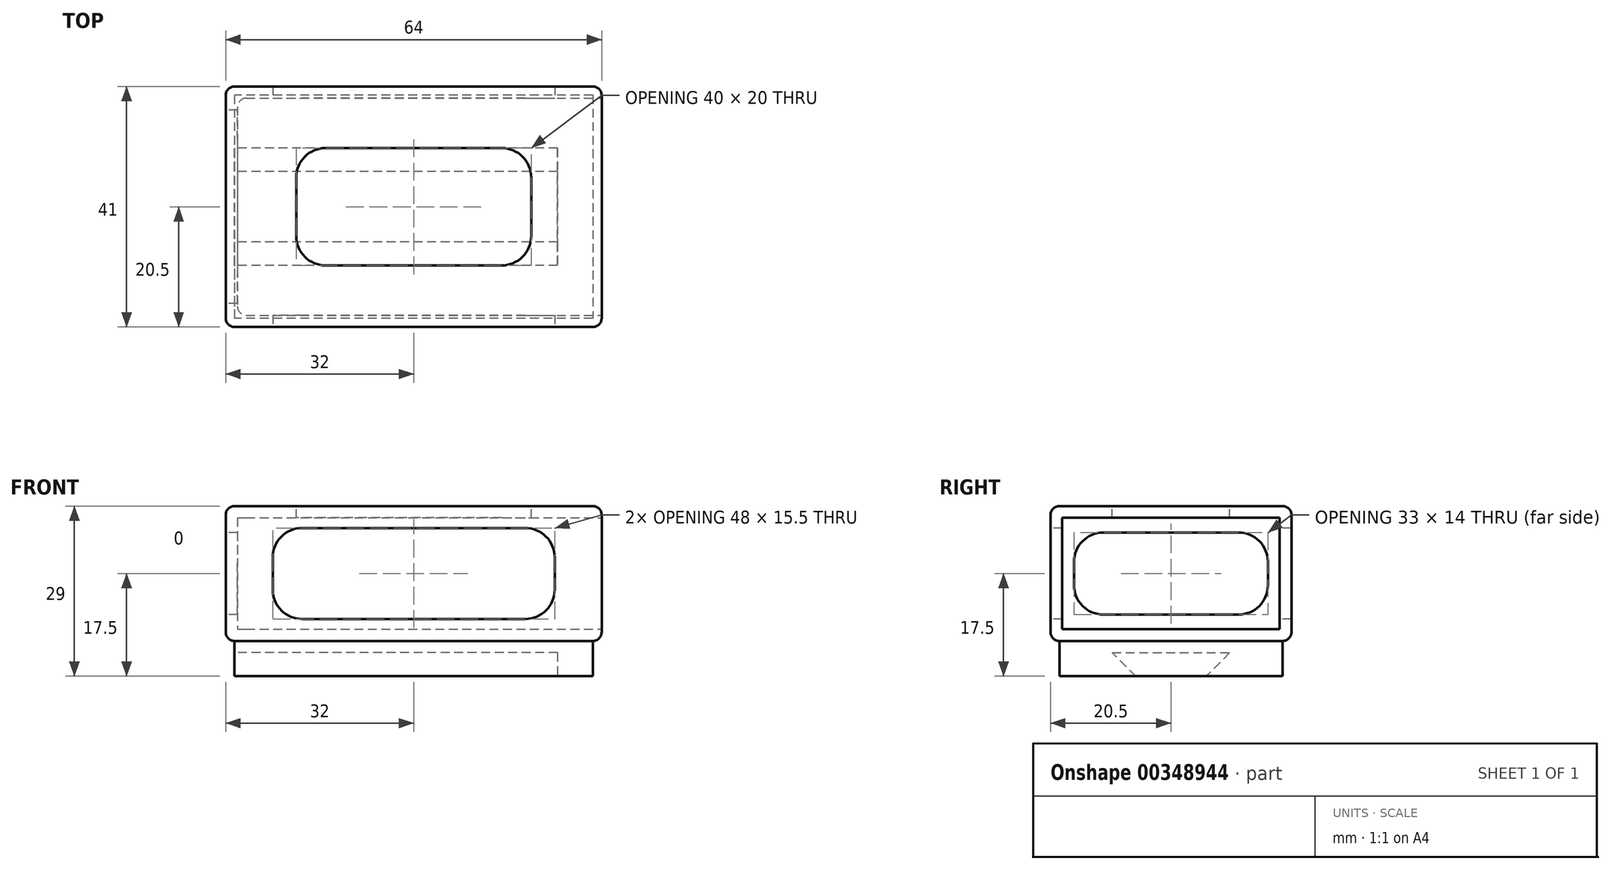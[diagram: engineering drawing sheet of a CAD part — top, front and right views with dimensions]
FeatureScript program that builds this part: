
annotation { "Feature Type Name" : "Feature", "Feature Type Description" : "" }
export const myFeature = defineFeature(function(context is Context, id is Id, definition is map)
    precondition{}
    {
        {
            var Q0;
            Q0=qCreatedBy(makeId("Top.planeOp"),FACE);
            var sketch = newSketch(context, id + "F0", { "sketchPlane" : qUnion([Q0])});
            skLineSegment(sketch, "E0.bottom", {"start": v(32, 20.5) * mm, "end": v(-32, 20.5) * mm});
            skLineSegment(sketch, "E0.top", {"start": v(32, -20.5) * mm, "end": v(-32, -20.5) * mm});
            skLineSegment(sketch, "E0.left", {"start": v(32, 20.5) * mm, "end": v(32, -20.5) * mm});
            skLineSegment(sketch, "E0.right", {"start": v(-32, 20.5) * mm, "end": v(-32, -20.5) * mm});
            skPoint(sketch, "E0.middle", {"position": v(0, 0) * mm});
            skSolve(sketch);
        }
        {
            var Q0;
            Q0=makeQuery(id+"F0.imprint","IMPRINT",FACE,{"disambiguationData":[TD([[makeQuery(id+"F0.imprint","IMPRINT",EDGE,{"derivedFrom":sQuery(id+"F0.wireOp",EDGE,"E0.bottom")}),1.0]])]});
            extrude(context, id + "F1", {"entities" : qUnion([Q0]), "depth" : 11.5 * mm});
        }
        {
            var Q0;
            Q0=makeQuery(id+"F1.opExtrude","CAP_EDGE",EDGE,{"disambiguationData":[OSD([sQuery(id+"F0.wireOp",EDGE,"E0.right")])],"isStart":false});
            var Q1;
            Q1=makeQuery(id+"F1.opExtrude","CAP_EDGE",EDGE,{"disambiguationData":[OSD([sQuery(id+"F0.wireOp",EDGE,"E0.top")])],"isStart":false});
            var Q2;
            Q2=makeQuery(id+"F1.opExtrude","CAP_EDGE",EDGE,{"disambiguationData":[OSD([sQuery(id+"F0.wireOp",EDGE,"E0.left")])],"isStart":false});
            var Q3;
            Q3=makeQuery(id+"F1.opExtrude","CAP_EDGE",EDGE,{"disambiguationData":[OSD([sQuery(id+"F0.wireOp",EDGE,"E0.bottom")])],"isStart":false});
            var Q4;
            Q4=makeQuery(id+"F1.opExtrude","SWEPT_EDGE",EDGE,{"disambiguationData":[OSD([sQuery(id+"F0.wireOp",EDGE,"E0.top"),sQuery(id+"F0.wireOp",EDGE,"E0.left")])]});
            var Q5;
            Q5=makeQuery(id+"F1.opExtrude","SWEPT_EDGE",EDGE,{"disambiguationData":[OSD([sQuery(id+"F0.wireOp",EDGE,"E0.bottom"),sQuery(id+"F0.wireOp",EDGE,"E0.left")])]});
            var Q6;
            Q6=makeQuery(id+"F1.opExtrude","SWEPT_EDGE",EDGE,{"disambiguationData":[OSD([sQuery(id+"F0.wireOp",EDGE,"E0.top"),sQuery(id+"F0.wireOp",EDGE,"E0.right")])]});
            var Q7;
            Q7=makeQuery(id+"F1.opExtrude","SWEPT_EDGE",EDGE,{"disambiguationData":[OSD([sQuery(id+"F0.wireOp",EDGE,"E0.bottom"),sQuery(id+"F0.wireOp",EDGE,"E0.right")])]});
            fillet(context, id + "F2", {"entities" : qUnion([Q0, Q1, Q2, Q3, Q4, Q5, Q6, Q7]), "radius" : 1.5 * mm, "tangentPropagation" : true, "allowEdgeOverflow" : false});
        }
        {
            var Q0;
            Q0=makeQuery(id+"F1.opExtrude","CAP_FACE",FACE,{"disambiguationData":[OSD([sQuery(id+"F0.wireOp",EDGE,"E0.bottom"),sQuery(id+"F0.wireOp",EDGE,"E0.top"),sQuery(id+"F0.wireOp",EDGE,"E0.left"),sQuery(id+"F0.wireOp",EDGE,"E0.right")])],"isStart":true});
            shell(context, id + "F3", {"entities" : qUnion([Q0]), "thickness" : 2 * mm});
        }
        {
            var Q0;
            Q0=makeQuery(id+"F3.opShell","OFFSET_EDGE",EDGE,{"disambiguationData":[OSD([sQuery(id+"F0.wireOp",EDGE,"E0.bottom"),sQuery(id+"F0.wireOp",EDGE,"E0.right")])]});
            var Q1;
            Q1=makeQuery(id+"F3.opShell","OFFSET_EDGE",EDGE,{"disambiguationData":[OSD([sQuery(id+"F0.wireOp",EDGE,"E0.top"),sQuery(id+"F0.wireOp",EDGE,"E0.right")])]});
            fillet(context, id + "F4", {"entities" : qUnion([Q0, Q1]), "radius" : 1.5 * mm, "tangentPropagation" : true, "allowEdgeOverflow" : false});
        }
        {
            var Q0;
            Q0=makeQuery(id+"F1.opExtrude","SWEPT_BODY",BODY,{"disambiguationData":[OSD([sQuery(id+"F0.wireOp",EDGE,"E0.bottom"),sQuery(id+"F0.wireOp",EDGE,"E0.top"),sQuery(id+"F0.wireOp",EDGE,"E0.left"),sQuery(id+"F0.wireOp",EDGE,"E0.right")])]});
            var Q1;
            Q1=qCreatedBy(makeId("Top.planeOp"),FACE);
            mirror(context, id + "F5", {"operationType" : NewBodyOperationType.ADD, "entities" : qUnion([Q0]), "mirrorPlane" : qUnion([Q1])});
        }
        {
            var Q0;
            {var subQ0=makeQuery(id+"F1.opExtrude","SWEPT_FACE",FACE,{"disambiguationData":[OSD([sQuery(id+"F0.wireOp",EDGE,"E0.top")])]});Q0=makeQuery(id+"F5.boolean.opBoolean","MERGE",FACE,{"derivedFrom":[subQ0,makeQuery(id+"F5.opPattern","COPY",FACE,{"derivedFrom":subQ0,"instanceName":"1"})]});}
            var sketch = newSketch(context, id + "F6", { "sketchPlane" : qUnion([Q0])});
            skLineSegment(sketch, "E1.bottom", {"start": v(24, -7.75) * mm, "end": v(-24, -7.75) * mm});
            skLineSegment(sketch, "E1.top", {"start": v(24, 7.75) * mm, "end": v(-24, 7.75) * mm});
            skLineSegment(sketch, "E1.left", {"start": v(24, -7.75) * mm, "end": v(24, 7.75) * mm});
            skLineSegment(sketch, "E1.right", {"start": v(-24, -7.75) * mm, "end": v(-24, 7.75) * mm});
            skPoint(sketch, "E1.middle", {"position": v(0, 0) * mm});
            skSolve(sketch);
        }
        {
            var Q0;
            Q0=makeQuery(id+"F6.imprint","IMPRINT",FACE,{"disambiguationData":[TD([[makeQuery(id+"F6.imprint","IMPRINT",EDGE,{"derivedFrom":sQuery(id+"F6.wireOp",EDGE,"E1.bottom")}),-1.0]])]});
            extrude(context, id + "F7", {"entities" : qUnion([Q0]), "operationType" : NewBodyOperationType.REMOVE, "endBound" : BoundingType.THROUGH_ALL, "oppositeDirection" : true, "depth" : 5 * mm});
        }
        {
            var Q0;
            {var subQ0=makeQuery(id+"F1.opExtrude","SWEPT_FACE",FACE,{"disambiguationData":[OSD([sQuery(id+"F0.wireOp",EDGE,"E0.right")])]});Q0=makeQuery(id+"F5.boolean.opBoolean","MERGE",FACE,{"derivedFrom":[subQ0,makeQuery(id+"F5.opPattern","COPY",FACE,{"derivedFrom":subQ0,"instanceName":"1"})]});}
            var sketch = newSketch(context, id + "F8", { "sketchPlane" : qUnion([Q0])});
            skLineSegment(sketch, "E2.bottom", {"start": v(16.5, 7) * mm, "end": v(-16.5, 7) * mm});
            skLineSegment(sketch, "E2.top", {"start": v(16.5, -7) * mm, "end": v(-16.5, -7) * mm});
            skLineSegment(sketch, "E2.left", {"start": v(16.5, 7) * mm, "end": v(16.5, -7) * mm});
            skLineSegment(sketch, "E2.right", {"start": v(-16.5, 7) * mm, "end": v(-16.5, -7) * mm});
            skPoint(sketch, "E2.middle", {"position": v(0, 0) * mm});
            skSolve(sketch);
        }
        {
            var Q0;
            Q0=makeQuery(id+"F8.imprint","IMPRINT",FACE,{"disambiguationData":[TD([[makeQuery(id+"F8.imprint","IMPRINT",EDGE,{"derivedFrom":sQuery(id+"F8.wireOp",EDGE,"E2.bottom")}),1.0]])]});
            extrude(context, id + "F9", {"entities" : qUnion([Q0]), "operationType" : NewBodyOperationType.REMOVE, "oppositeDirection" : true, "depth" : 5 * mm});
        }
        {
            var Q0;
            {var subQ0=sQuery(id+"F0.wireOp",EDGE,"E0.left");var subQ2=makeQuery(id+"F1.opExtrude","SWEPT_FACE",FACE,{"disambiguationData":[OSD([subQ0])]});var subQ3=sQuery(id+"F8.wireOp",EDGE,"E2.right");var subQ4=sQuery(id+"F8.wireOp",EDGE,"E2.top");Q0=makeQuery(id+"F9.boolean.opBoolean","COPY",EDGE,{"disambiguationData":[TD([subQ2])],"derivedFrom":makeQuery(id+"F9.opExtrude","SWEPT_EDGE",EDGE,{"disambiguationData":[OSD([subQ4,subQ3])]})});}
            var Q1;
            {var subQ0=sQuery(id+"F0.wireOp",EDGE,"E0.right");var subQ2=makeQuery(id+"F1.opExtrude","SWEPT_FACE",FACE,{"disambiguationData":[OSD([subQ0])]});var subQ3=sQuery(id+"F8.wireOp",EDGE,"E2.top");var subQ4=sQuery(id+"F8.wireOp",EDGE,"E2.right");Q1=makeQuery(id+"F9.boolean.opBoolean","COPY",EDGE,{"disambiguationData":[TD([subQ2])],"derivedFrom":makeQuery(id+"F9.opExtrude","SWEPT_EDGE",EDGE,{"disambiguationData":[OSD([subQ3,subQ4])]})});}
            var Q2;
            {var subQ0=sQuery(id+"F0.wireOp",EDGE,"E0.left");var subQ2=makeQuery(id+"F1.opExtrude","SWEPT_FACE",FACE,{"disambiguationData":[OSD([subQ0])]});var subQ3=sQuery(id+"F8.wireOp",EDGE,"E2.top");var subQ4=sQuery(id+"F8.wireOp",EDGE,"E2.left");Q2=makeQuery(id+"F9.boolean.opBoolean","COPY",EDGE,{"disambiguationData":[TD([subQ2])],"derivedFrom":makeQuery(id+"F9.opExtrude","SWEPT_EDGE",EDGE,{"disambiguationData":[OSD([subQ3,subQ4])]})});}
            var Q3;
            {var subQ0=sQuery(id+"F0.wireOp",EDGE,"E0.right");var subQ2=makeQuery(id+"F1.opExtrude","SWEPT_FACE",FACE,{"disambiguationData":[OSD([subQ0])]});var subQ3=sQuery(id+"F8.wireOp",EDGE,"E2.top");var subQ4=sQuery(id+"F8.wireOp",EDGE,"E2.left");Q3=makeQuery(id+"F9.boolean.opBoolean","COPY",EDGE,{"disambiguationData":[TD([subQ2])],"derivedFrom":makeQuery(id+"F9.opExtrude","SWEPT_EDGE",EDGE,{"disambiguationData":[OSD([subQ3,subQ4])]})});}
            var Q4;
            {var subQ0=sQuery(id+"F0.wireOp",EDGE,"E0.left");var subQ2=makeQuery(id+"F1.opExtrude","SWEPT_FACE",FACE,{"disambiguationData":[OSD([subQ0])]});var subQ3=sQuery(id+"F8.wireOp",EDGE,"E2.right");var subQ4=sQuery(id+"F8.wireOp",EDGE,"E2.bottom");Q4=makeQuery(id+"F9.boolean.opBoolean","COPY",EDGE,{"disambiguationData":[TD([subQ2])],"derivedFrom":makeQuery(id+"F9.opExtrude","SWEPT_EDGE",EDGE,{"disambiguationData":[OSD([subQ4,subQ3])]})});}
            var Q5;
            {var subQ0=sQuery(id+"F0.wireOp",EDGE,"E0.right");var subQ2=makeQuery(id+"F1.opExtrude","SWEPT_FACE",FACE,{"disambiguationData":[OSD([subQ0])]});var subQ3=sQuery(id+"F8.wireOp",EDGE,"E2.bottom");var subQ4=sQuery(id+"F8.wireOp",EDGE,"E2.right");Q5=makeQuery(id+"F9.boolean.opBoolean","COPY",EDGE,{"disambiguationData":[TD([subQ2])],"derivedFrom":makeQuery(id+"F9.opExtrude","SWEPT_EDGE",EDGE,{"disambiguationData":[OSD([subQ3,subQ4])]})});}
            var Q6;
            {var subQ0=sQuery(id+"F0.wireOp",EDGE,"E0.right");var subQ2=sQuery(id+"F8.wireOp",EDGE,"E2.bottom");var subQ3=makeQuery(id+"F1.opExtrude","SWEPT_FACE",FACE,{"disambiguationData":[OSD([subQ0])]});var subQ4=sQuery(id+"F8.wireOp",EDGE,"E2.left");Q6=makeQuery(id+"F9.boolean.opBoolean","COPY",EDGE,{"disambiguationData":[TD([subQ3])],"derivedFrom":makeQuery(id+"F9.opExtrude","SWEPT_EDGE",EDGE,{"disambiguationData":[OSD([subQ2,subQ4])]})});}
            var Q7;
            {var subQ0=sQuery(id+"F0.wireOp",EDGE,"E0.left");var subQ2=makeQuery(id+"F1.opExtrude","SWEPT_FACE",FACE,{"disambiguationData":[OSD([subQ0])]});var subQ3=sQuery(id+"F8.wireOp",EDGE,"E2.bottom");var subQ4=sQuery(id+"F8.wireOp",EDGE,"E2.left");Q7=makeQuery(id+"F9.boolean.opBoolean","COPY",EDGE,{"disambiguationData":[TD([subQ2])],"derivedFrom":makeQuery(id+"F9.opExtrude","SWEPT_EDGE",EDGE,{"disambiguationData":[OSD([subQ3,subQ4])]})});}
            fillet(context, id + "F10", {"entities" : qUnion([Q0, Q1, Q2, Q3, Q4, Q5, Q6, Q7]), "radius" : 5 * mm, "tangentPropagation" : true, "allowEdgeOverflow" : false});
        }
        {
            var Q0;
            {var subQ0=sQuery(id+"F0.wireOp",EDGE,"E0.top");var subQ2=makeQuery(id+"F1.opExtrude","SWEPT_FACE",FACE,{"disambiguationData":[OSD([subQ0])]});var subQ3=sQuery(id+"F6.wireOp",EDGE,"E1.top");var subQ4=sQuery(id+"F6.wireOp",EDGE,"E1.right");Q0=makeQuery(id+"F7.boolean.opBoolean","COPY",EDGE,{"disambiguationData":[TD([subQ2])],"derivedFrom":makeQuery(id+"F7.opExtrude","SWEPT_EDGE",EDGE,{"disambiguationData":[OSD([subQ3,subQ4])]})});}
            var Q1;
            {var subQ0=sQuery(id+"F0.wireOp",EDGE,"E0.top");var subQ2=makeQuery(id+"F1.opExtrude","SWEPT_FACE",FACE,{"disambiguationData":[OSD([subQ0])]});var subQ3=sQuery(id+"F6.wireOp",EDGE,"E1.left");var subQ4=sQuery(id+"F6.wireOp",EDGE,"E1.top");Q1=makeQuery(id+"F7.boolean.opBoolean","COPY",EDGE,{"disambiguationData":[TD([subQ2])],"derivedFrom":makeQuery(id+"F7.opExtrude","SWEPT_EDGE",EDGE,{"disambiguationData":[OSD([subQ4,subQ3])]})});}
            var Q2;
            {var subQ0=sQuery(id+"F0.wireOp",EDGE,"E0.top");var subQ2=sQuery(id+"F6.wireOp",EDGE,"E1.bottom");var subQ3=makeQuery(id+"F1.opExtrude","SWEPT_FACE",FACE,{"disambiguationData":[OSD([subQ0])]});var subQ4=sQuery(id+"F6.wireOp",EDGE,"E1.right");Q2=makeQuery(id+"F7.boolean.opBoolean","COPY",EDGE,{"disambiguationData":[TD([subQ3])],"derivedFrom":makeQuery(id+"F7.opExtrude","SWEPT_EDGE",EDGE,{"disambiguationData":[OSD([subQ2,subQ4])]})});}
            var Q3;
            {var subQ0=sQuery(id+"F0.wireOp",EDGE,"E0.top");var subQ2=sQuery(id+"F6.wireOp",EDGE,"E1.bottom");var subQ3=makeQuery(id+"F1.opExtrude","SWEPT_FACE",FACE,{"disambiguationData":[OSD([subQ0])]});var subQ4=sQuery(id+"F6.wireOp",EDGE,"E1.left");Q3=makeQuery(id+"F7.boolean.opBoolean","COPY",EDGE,{"disambiguationData":[TD([subQ3])],"derivedFrom":makeQuery(id+"F7.opExtrude","SWEPT_EDGE",EDGE,{"disambiguationData":[OSD([subQ2,subQ4])]})});}
            fillet(context, id + "F11", {"entities" : qUnion([Q0, Q1, Q2, Q3]), "radius" : 5 * mm, "tangentPropagation" : true, "allowEdgeOverflow" : false});
        }
        {
            var Q0;
            {var subQ0=sQuery(id+"F0.wireOp",EDGE,"E0.bottom");var subQ1=makeQuery(id+"F1.opExtrude","SWEPT_FACE",FACE,{"disambiguationData":[OSD([subQ0])]});var subQ3=sQuery(id+"F6.wireOp",EDGE,"E1.top");var subQ4=sQuery(id+"F6.wireOp",EDGE,"E1.left");Q0=makeQuery(id+"F7.boolean.opBoolean","COPY",EDGE,{"disambiguationData":[TD([subQ1])],"derivedFrom":makeQuery(id+"F7.opExtrude","SWEPT_EDGE",EDGE,{"disambiguationData":[OSD([subQ3,subQ4])]})});}
            var Q1;
            {var subQ0=sQuery(id+"F0.wireOp",EDGE,"E0.bottom");var subQ1=makeQuery(id+"F1.opExtrude","SWEPT_FACE",FACE,{"disambiguationData":[OSD([subQ0])]});var subQ3=sQuery(id+"F6.wireOp",EDGE,"E1.bottom");var subQ4=sQuery(id+"F6.wireOp",EDGE,"E1.left");Q1=makeQuery(id+"F7.boolean.opBoolean","COPY",EDGE,{"disambiguationData":[TD([subQ1])],"derivedFrom":makeQuery(id+"F7.opExtrude","SWEPT_EDGE",EDGE,{"disambiguationData":[OSD([subQ3,subQ4])]})});}
            var Q2;
            {var subQ0=sQuery(id+"F0.wireOp",EDGE,"E0.bottom");var subQ1=makeQuery(id+"F1.opExtrude","SWEPT_FACE",FACE,{"disambiguationData":[OSD([subQ0])]});var subQ3=sQuery(id+"F6.wireOp",EDGE,"E1.right");var subQ4=sQuery(id+"F6.wireOp",EDGE,"E1.bottom");Q2=makeQuery(id+"F7.boolean.opBoolean","COPY",EDGE,{"disambiguationData":[TD([subQ1])],"derivedFrom":makeQuery(id+"F7.opExtrude","SWEPT_EDGE",EDGE,{"disambiguationData":[OSD([subQ4,subQ3])]})});}
            var Q3;
            {var subQ0=sQuery(id+"F0.wireOp",EDGE,"E0.bottom");var subQ1=makeQuery(id+"F1.opExtrude","SWEPT_FACE",FACE,{"disambiguationData":[OSD([subQ0])]});var subQ3=sQuery(id+"F6.wireOp",EDGE,"E1.right");var subQ4=sQuery(id+"F6.wireOp",EDGE,"E1.top");Q3=makeQuery(id+"F7.boolean.opBoolean","COPY",EDGE,{"disambiguationData":[TD([subQ1])],"derivedFrom":makeQuery(id+"F7.opExtrude","SWEPT_EDGE",EDGE,{"disambiguationData":[OSD([subQ4,subQ3])]})});}
            fillet(context, id + "F12", {"entities" : qUnion([Q0, Q1, Q2, Q3]), "radius" : 5 * mm, "tangentPropagation" : true, "allowEdgeOverflow" : false});
        }
        {
            var Q0;
            Q0=makeQuery(id+"F1.opExtrude","CAP_FACE",FACE,{"disambiguationData":[OSD([sQuery(id+"F0.wireOp",EDGE,"E0.bottom"),sQuery(id+"F0.wireOp",EDGE,"E0.top"),sQuery(id+"F0.wireOp",EDGE,"E0.left"),sQuery(id+"F0.wireOp",EDGE,"E0.right")])],"isStart":false});
            var sketch = newSketch(context, id + "F13", { "sketchPlane" : qUnion([Q0])});
            skLineSegment(sketch, "E3.bottom", {"start": v(20, -10) * mm, "end": v(-20, -10) * mm});
            skLineSegment(sketch, "E3.top", {"start": v(20, 10) * mm, "end": v(-20, 10) * mm});
            skLineSegment(sketch, "E3.left", {"start": v(20, -10) * mm, "end": v(20, 10) * mm});
            skLineSegment(sketch, "E3.right", {"start": v(-20, -10) * mm, "end": v(-20, 10) * mm});
            skPoint(sketch, "E3.middle", {"position": v(0, 0) * mm});
            skSolve(sketch);
        }
        {
            var Q0;
            Q0=makeQuery(id+"F13.imprint","IMPRINT",FACE,{"disambiguationData":[TD([[makeQuery(id+"F13.imprint","IMPRINT",EDGE,{"derivedFrom":sQuery(id+"F13.wireOp",EDGE,"E3.bottom")}),-1.0]])]});
            extrude(context, id + "F14", {"entities" : qUnion([Q0]), "operationType" : NewBodyOperationType.REMOVE, "oppositeDirection" : true, "depth" : 5 * mm});
        }
        {
            var Q0;
            Q0=makeQuery(id+"F14.boolean.opBoolean","COPY",EDGE,{"derivedFrom":makeQuery(id+"F14.opExtrude","SWEPT_EDGE",EDGE,{"disambiguationData":[OSD([sQuery(id+"F13.wireOp",EDGE,"E3.top"),sQuery(id+"F13.wireOp",EDGE,"E3.right")])]})});
            var Q1;
            Q1=makeQuery(id+"F14.boolean.opBoolean","COPY",EDGE,{"derivedFrom":makeQuery(id+"F14.opExtrude","SWEPT_EDGE",EDGE,{"disambiguationData":[OSD([sQuery(id+"F13.wireOp",EDGE,"E3.bottom"),sQuery(id+"F13.wireOp",EDGE,"E3.right")])]})});
            var Q2;
            Q2=makeQuery(id+"F14.boolean.opBoolean","COPY",EDGE,{"derivedFrom":makeQuery(id+"F14.opExtrude","SWEPT_EDGE",EDGE,{"disambiguationData":[OSD([sQuery(id+"F13.wireOp",EDGE,"E3.bottom"),sQuery(id+"F13.wireOp",EDGE,"E3.left")])]})});
            var Q3;
            Q3=makeQuery(id+"F14.boolean.opBoolean","COPY",EDGE,{"derivedFrom":makeQuery(id+"F14.opExtrude","SWEPT_EDGE",EDGE,{"disambiguationData":[OSD([sQuery(id+"F13.wireOp",EDGE,"E3.top"),sQuery(id+"F13.wireOp",EDGE,"E3.left")])]})});
            fillet(context, id + "F15", {"entities" : qUnion([Q0, Q1, Q2, Q3]), "radius" : 5 * mm, "tangentPropagation" : true, "allowEdgeOverflow" : false});
        }
        {
            var Q0;
            {var subQ0=makeQuery(id+"F1.opExtrude","SWEPT_FACE",FACE,{"disambiguationData":[OSD([sQuery(id+"F0.wireOp",EDGE,"E0.left")])]});Q0=makeQuery(id+"F5.boolean.opBoolean","MERGE",FACE,{"derivedFrom":[subQ0,makeQuery(id+"F5.opPattern","COPY",FACE,{"derivedFrom":subQ0,"instanceName":"1"})]});}
            var sketch = newSketch(context, id + "F16", { "sketchPlane" : qUnion([Q0])});
            skLineSegment(sketch, "E4.bottom", {"start": v(18.5, -9.5) * mm, "end": v(-18.5, -9.5) * mm});
            skLineSegment(sketch, "E4.top", {"start": v(18.5, 9.5) * mm, "end": v(-18.5, 9.5) * mm});
            skLineSegment(sketch, "E4.left", {"start": v(18.5, -9.5) * mm, "end": v(18.5, 9.5) * mm});
            skLineSegment(sketch, "E4.right", {"start": v(-18.5, -9.5) * mm, "end": v(-18.5, 9.5) * mm});
            skPoint(sketch, "E4.middle", {"position": v(0, 0) * mm});
            skSolve(sketch);
        }
        {
            var Q0;
            Q0=makeQuery(id+"F16.imprint","IMPRINT",FACE,{"disambiguationData":[TD([[makeQuery(id+"F16.imprint","IMPRINT",EDGE,{"derivedFrom":sQuery(id+"F16.wireOp",EDGE,"E4.bottom")}),-1.0]])]});
            extrude(context, id + "F17", {"entities" : qUnion([Q0]), "operationType" : NewBodyOperationType.REMOVE, "oppositeDirection" : true, "depth" : 5 * mm});
        }
        {
            var Q0;
            Q0=makeQuery(id+"F5.opPattern","COPY",FACE,{"derivedFrom":makeQuery(id+"F1.opExtrude","CAP_FACE",FACE,{"disambiguationData":[OSD([sQuery(id+"F0.wireOp",EDGE,"E0.bottom"),sQuery(id+"F0.wireOp",EDGE,"E0.top"),sQuery(id+"F0.wireOp",EDGE,"E0.left"),sQuery(id+"F0.wireOp",EDGE,"E0.right")])],"isStart":false}),"instanceName":"1"});
            var sketch = newSketch(context, id + "F18", { "sketchPlane" : qUnion([Q0])});
            skLineSegment(sketch, "E5.bottom", {"start": v(30.5, -19) * mm, "end": v(-30.5, -19) * mm});
            skLineSegment(sketch, "E5.top", {"start": v(30.5, 19) * mm, "end": v(-30.5, 19) * mm});
            skLineSegment(sketch, "E5.left", {"start": v(30.5, -19) * mm, "end": v(30.5, 19) * mm});
            skLineSegment(sketch, "E5.right", {"start": v(-30.5, -19) * mm, "end": v(-30.5, 19) * mm});
            skPoint(sketch, "E5.middle", {"position": v(0, 0) * mm});
            skSolve(sketch);
        }
        {
            var Q0;
            Q0=makeQuery(id+"F18.imprint","IMPRINT",FACE,{"disambiguationData":[TD([[makeQuery(id+"F18.imprint","IMPRINT",EDGE,{"derivedFrom":sQuery(id+"F18.wireOp",EDGE,"E5.bottom")}),-1.0]])]});
            extrude(context, id + "F19", {"entities" : qUnion([Q0]), "operationType" : NewBodyOperationType.ADD, "depth" : 6 * mm});
        }
        {
            var Q0;
            Q0=makeQuery(id+"F19.opExtrude","SWEPT_FACE",FACE,{"disambiguationData":[OSD([sQuery(id+"F18.wireOp",EDGE,"E5.right")])]});
            var sketch = newSketch(context, id + "F20", { "sketchPlane" : qUnion([Q0])});
            skLineSegment(sketch, "E6.bottom", {"start": v(10, -21.5) * mm, "end": v(-10, -21.5) * mm, "construction": true});
            skLineSegment(sketch, "E6.top", {"start": v(10, -13.5) * mm, "end": v(-10, -13.5) * mm, "construction": true});
            skLineSegment(sketch, "E6.left", {"start": v(10, -21.5) * mm, "end": v(10, -13.5) * mm, "construction": true});
            skLineSegment(sketch, "E6.right", {"start": v(-10, -21.5) * mm, "end": v(-10, -13.5) * mm, "construction": true});
            skPoint(sketch, "E6.middle", {"position": v(0, -17.5) * mm});
            skLineSegment(sketch, "E7.bottom", {"start": v(6, -21.5) * mm, "end": v(-6, -21.5) * mm, "construction": true});
            skLineSegment(sketch, "E7.top", {"start": v(6, -13.5) * mm, "end": v(-6, -13.5) * mm, "construction": true});
            skLineSegment(sketch, "E7.left", {"start": v(6, -21.5) * mm, "end": v(6, -13.5) * mm, "construction": true});
            skLineSegment(sketch, "E7.right", {"start": v(-6, -21.5) * mm, "end": v(-6, -13.5) * mm, "construction": true});
            skPoint(sketch, "E8", {"position": v(-6, -17.5) * mm});
            skPoint(sketch, "E9", {"position": v(6, -17.5) * mm});
            skLineSegment(sketch, "E10", {"start": v(6, -17.5) * mm, "end": v(-6, -17.5) * mm, "construction": true});
            skLineSegment(sketch, "E11", {"start": v(6, -17.5) * mm, "end": v(-6, -17.5) * mm});
            skLineSegment(sketch, "E12", {"start": v(-10, -13.5) * mm, "end": v(-6, -17.5) * mm});
            skLineSegment(sketch, "E13", {"start": v(6, -17.5) * mm, "end": v(10, -13.5) * mm});
            skLineSegment(sketch, "E14", {"start": v(10, -13.5) * mm, "end": v(-10, -13.5) * mm});
            skSolve(sketch);
        }
        {
            var Q0;
            Q0=makeQuery(id+"F20.imprint","IMPRINT",FACE,{"disambiguationData":[TD([[makeQuery(id+"F20.imprint","IMPRINT",EDGE,{"derivedFrom":sQuery(id+"F20.wireOp",EDGE,"E11")}),1.0]])]});
            extrude(context, id + "F21", {"entities" : qUnion([Q0]), "operationType" : NewBodyOperationType.REMOVE, "oppositeDirection" : true, "depth" : 55 * mm});
        }
    });
